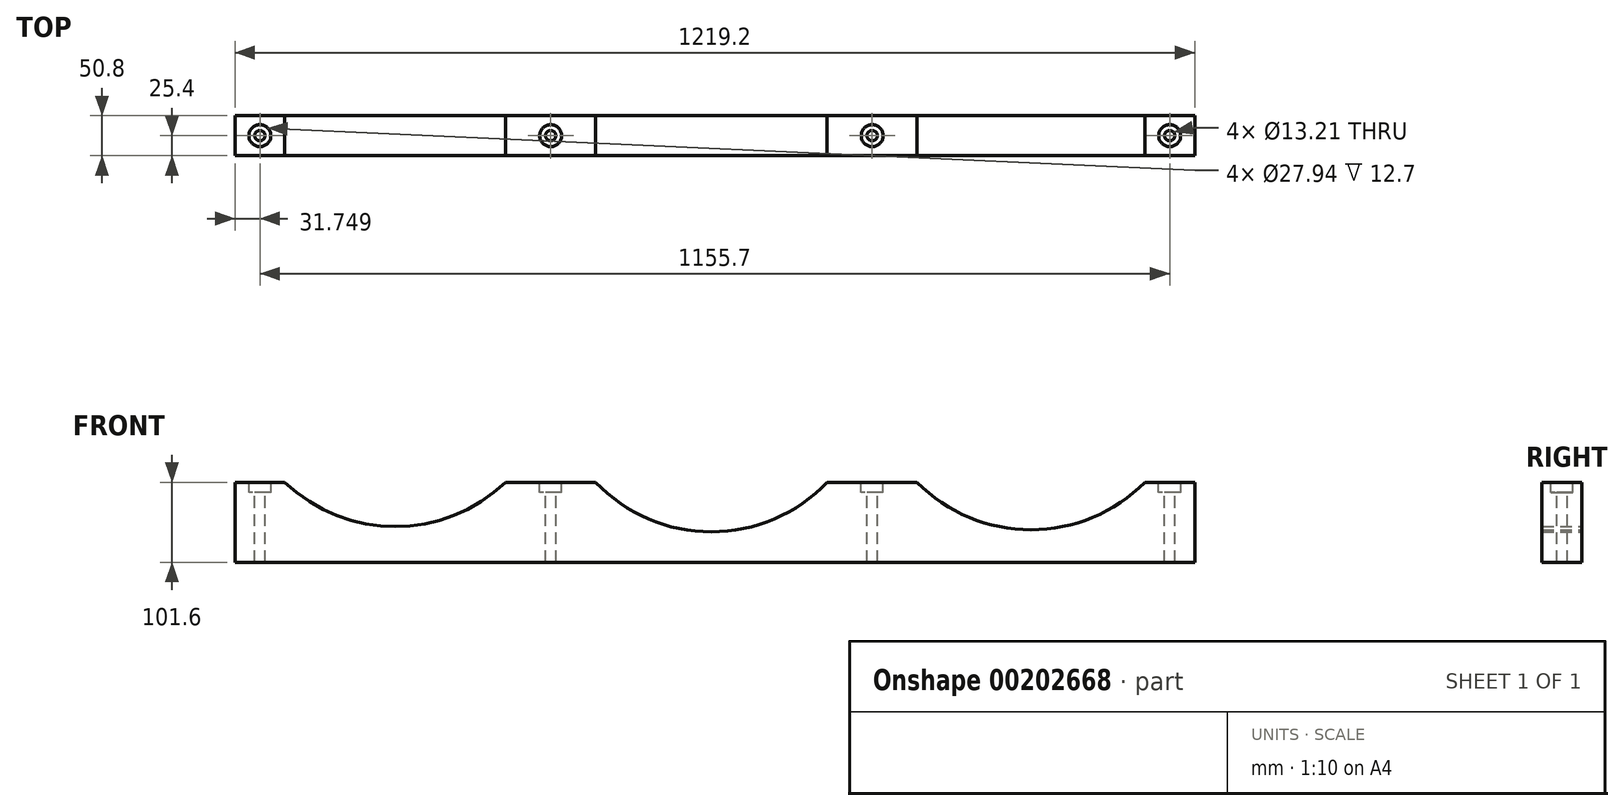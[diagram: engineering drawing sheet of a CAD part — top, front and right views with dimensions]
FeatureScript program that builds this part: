
annotation { "Feature Type Name" : "Feature", "Feature Type Description" : "" }
export const myFeature = defineFeature(function(context is Context, id is Id, definition is map)
    precondition{}
    {
        {
            var Q0;
            Q0=qCreatedBy(makeId("Front.planeOp"),FACE);
            var sketch = newSketch(context, id + "F0", { "sketchPlane" : qUnion([Q0])});
            skLineSegment(sketch, "E0", {"start": v(-153.2, -151.35) * mm, "end": v(-216.7, -151.35) * mm});
            skLineSegment(sketch, "E1", {"start": v(-216.7, -151.35) * mm, "end": v(-216.7, -252.95) * mm});
            skLineSegment(sketch, "E2", {"start": v(-216.7, -252.95) * mm, "end": v(1002.5, -252.95) * mm});
            skLineSegment(sketch, "E3", {"start": v(1002.5, -252.95) * mm, "end": v(1002.5, -151.35) * mm});
            skLineSegment(sketch, "E4", {"start": v(1002.5, -151.35) * mm, "end": v(939, -151.35) * mm});
            skLineSegment(sketch, "E5", {"start": v(127.27, -151.35) * mm, "end": v(241.57, -151.35) * mm});
            skLineSegment(sketch, "E6", {"start": v(535.7, -151.35) * mm, "end": v(650, -151.35) * mm});
            skArc(sketch, "E7", {"start": v(-153.2, -151.35) * mm, "mid": v(-12.96, -207.5) * mm, "end": v(127.27, -151.35) * mm});
            skArc(sketch, "E8", {"start": v(241.57, -151.35) * mm, "mid": v(388.63, -214.33) * mm, "end": v(535.7, -151.35) * mm});
            skArc(sketch, "E9", {"start": v(650, -151.35) * mm, "mid": v(794.5, -211.69) * mm, "end": v(939, -151.35) * mm});
            skSolve(sketch);
        }
        {
            var Q0;
            Q0 = qSketchRegion(id + "F0", true);
            extrude(context, id + "F1", {"entities" : qUnion([Q0]), "endBound" : BoundingType.SYMMETRIC, "depth" : 50.8 * mm});
        }
        {
            var Q0;
            Q0=makeQuery(id+"F1.opExtrude","SWEPT_FACE",FACE,{"disambiguationData":[OSD([sQuery(id+"F0.wireOp",EDGE,"E0")])]});
            var sketch = newSketch(context, id + "F2", { "sketchPlane" : qUnion([Q0])});
            skCircle(sketch, "E10", {"center": v(-184.95, 0) * mm, "radius": 6.6 * mm});
            skPoint(sketch, "E10.centerSnap0", {"position": v(-184.95, 25.4) * mm});
            skPoint(sketch, "E10.centerSnap1", {"position": v(-216.7, 0) * mm});
            skSolve(sketch);
        }
        {
            var Q0;
            Q0 = qSketchRegion(id + "F2", true);
            extrude(context, id + "F3", {"entities" : qUnion([Q0]), "operationType" : NewBodyOperationType.REMOVE, "endBound" : BoundingType.THROUGH_ALL, "oppositeDirection" : true, "depth" : 25.4 * mm});
        }
        {
            var Q0;
            Q0=makeQuery(id+"F1.opExtrude","SWEPT_FACE",FACE,{"disambiguationData":[OSD([sQuery(id+"F0.wireOp",EDGE,"E0")])]});
            var sketch = newSketch(context, id + "F4", { "sketchPlane" : qUnion([Q0])});
            skCircle(sketch, "E11", {"center": v(-184.95, 0) * mm, "radius": 13.97 * mm});
            skSolve(sketch);
        }
        {
            var Q0;
            Q0 = qSketchRegion(id + "F4", true);
            extrude(context, id + "F5", {"entities" : qUnion([Q0]), "operationType" : NewBodyOperationType.REMOVE, "oppositeDirection" : true, "depth" : 12.7 * mm});
        }
        {
            var Q0;
            Q0=makeQuery(id+"F1.opExtrude","SWEPT_FACE",FACE,{"disambiguationData":[OSD([sQuery(id+"F0.wireOp",EDGE,"E5")])]});
            var sketch = newSketch(context, id + "F6", { "sketchPlane" : qUnion([Q0])});
            skCircle(sketch, "E12", {"center": v(184.42, 0) * mm, "radius": 6.6 * mm});
            skPoint(sketch, "E12.centerSnap0", {"position": v(127.27, 0) * mm});
            skPoint(sketch, "E12.centerSnap1", {"position": v(184.42, 25.4) * mm});
            skSolve(sketch);
        }
        {
            var Q0;
            Q0 = qSketchRegion(id + "F6", true);
            extrude(context, id + "F7", {"entities" : qUnion([Q0]), "operationType" : NewBodyOperationType.REMOVE, "endBound" : BoundingType.THROUGH_ALL, "oppositeDirection" : true, "depth" : 25.4 * mm});
        }
        {
            var Q0;
            Q0=makeQuery(id+"F1.opExtrude","SWEPT_FACE",FACE,{"disambiguationData":[OSD([sQuery(id+"F0.wireOp",EDGE,"E5")])]});
            var sketch = newSketch(context, id + "F8", { "sketchPlane" : qUnion([Q0])});
            skCircle(sketch, "E13", {"center": v(184.42, 0) * mm, "radius": 13.97 * mm});
            skSolve(sketch);
        }
        {
            var Q0;
            Q0 = qSketchRegion(id + "F8", true);
            extrude(context, id + "F9", {"entities" : qUnion([Q0]), "operationType" : NewBodyOperationType.REMOVE, "oppositeDirection" : true, "depth" : 12.7 * mm});
        }
        {
            var Q0;
            Q0=makeQuery(id+"F1.opExtrude","SWEPT_FACE",FACE,{"disambiguationData":[OSD([sQuery(id+"F0.wireOp",EDGE,"E6")])]});
            var sketch = newSketch(context, id + "F10", { "sketchPlane" : qUnion([Q0])});
            skCircle(sketch, "E14", {"center": v(592.84, 0) * mm, "radius": 6.6 * mm});
            skPoint(sketch, "E14.centerSnap0", {"position": v(535.7, 0) * mm});
            skPoint(sketch, "E14.centerSnap1", {"position": v(592.84, 25.4) * mm});
            skSolve(sketch);
        }
        {
            var Q0;
            Q0 = qSketchRegion(id + "F10", true);
            extrude(context, id + "F11", {"entities" : qUnion([Q0]), "operationType" : NewBodyOperationType.REMOVE, "endBound" : BoundingType.THROUGH_ALL, "oppositeDirection" : true, "depth" : 25.4 * mm});
        }
        {
            var Q0;
            Q0=makeQuery(id+"F1.opExtrude","SWEPT_FACE",FACE,{"disambiguationData":[OSD([sQuery(id+"F0.wireOp",EDGE,"E6")])]});
            var sketch = newSketch(context, id + "F12", { "sketchPlane" : qUnion([Q0])});
            skCircle(sketch, "E15", {"center": v(592.84, 0) * mm, "radius": 13.97 * mm});
            skSolve(sketch);
        }
        {
            var Q0;
            Q0 = qSketchRegion(id + "F12", true);
            extrude(context, id + "F13", {"entities" : qUnion([Q0]), "operationType" : NewBodyOperationType.REMOVE, "oppositeDirection" : true, "depth" : 12.7 * mm});
        }
        {
            var Q0;
            Q0=makeQuery(id+"F1.opExtrude","SWEPT_FACE",FACE,{"disambiguationData":[OSD([sQuery(id+"F0.wireOp",EDGE,"E4")])]});
            var sketch = newSketch(context, id + "F14", { "sketchPlane" : qUnion([Q0])});
            skCircle(sketch, "E16", {"center": v(970.75, 0) * mm, "radius": 6.6 * mm});
            skPoint(sketch, "E16.centerSnap0", {"position": v(939, 0) * mm});
            skPoint(sketch, "E16.centerSnap1", {"position": v(970.75, 25.4) * mm});
            skSolve(sketch);
        }
        {
            var Q0;
            Q0 = qSketchRegion(id + "F14", true);
            extrude(context, id + "F15", {"entities" : qUnion([Q0]), "operationType" : NewBodyOperationType.REMOVE, "endBound" : BoundingType.THROUGH_ALL, "oppositeDirection" : true, "depth" : 25.4 * mm});
        }
        {
            var Q0;
            Q0=makeQuery(id+"F1.opExtrude","SWEPT_FACE",FACE,{"disambiguationData":[OSD([sQuery(id+"F0.wireOp",EDGE,"E4")])]});
            var sketch = newSketch(context, id + "F16", { "sketchPlane" : qUnion([Q0])});
            skCircle(sketch, "E17", {"center": v(970.75, 0) * mm, "radius": 13.97 * mm});
            skSolve(sketch);
        }
        {
            var Q0;
            Q0 = qSketchRegion(id + "F16", true);
            extrude(context, id + "F17", {"entities" : qUnion([Q0]), "operationType" : NewBodyOperationType.REMOVE, "oppositeDirection" : true, "depth" : 12.7 * mm});
        }
    });
